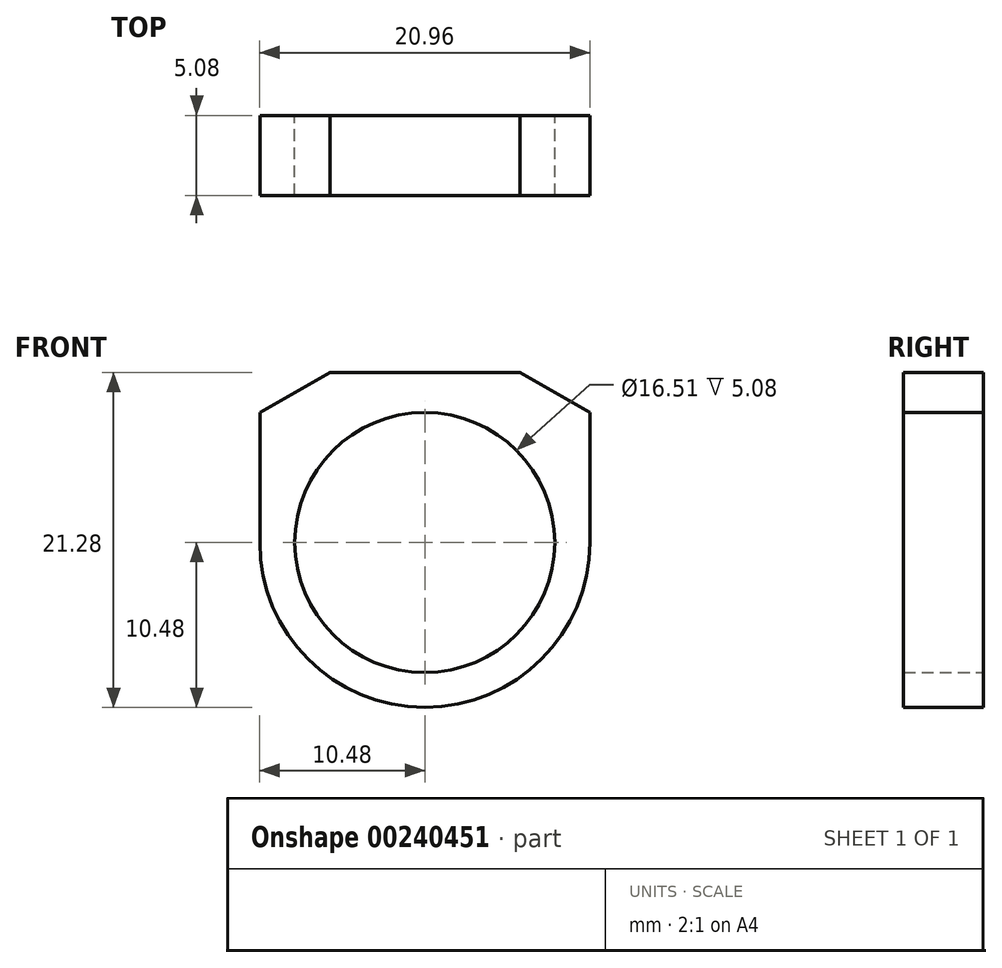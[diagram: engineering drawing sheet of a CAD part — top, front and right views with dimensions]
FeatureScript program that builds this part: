
annotation { "Feature Type Name" : "Feature", "Feature Type Description" : "" }
export const myFeature = defineFeature(function(context is Context, id is Id, definition is map)
    precondition{}
    {
        {
            var Q0;
            Q0=qCreatedBy(makeId("Front.planeOp"),FACE);
            var sketch = newSketch(context, id + "F0", { "sketchPlane" : qUnion([Q0])});
            skCircle(sketch, "E0", {"center": v(0, 0) * mm, "radius": 8.26 * mm});
            skCircle(sketch, "E1", {"center": v(0, 0) * mm, "radius": 10.48 * mm});
            skLineSegment(sketch, "E2", {"start": v(-10.48, 0) * mm, "end": v(-10.48, 8.26) * mm});
            skLineSegment(sketch, "E3", {"start": v(10.48, 0) * mm, "end": v(10.48, 8.26) * mm});
            skLineSegment(sketch, "E4", {"start": v(-10.48, 8.26) * mm, "end": v(-6.03, 10.8) * mm});
            skLineSegment(sketch, "E5", {"start": v(-6.03, 10.8) * mm, "end": v(6.03, 10.8) * mm});
            skLineSegment(sketch, "E6", {"start": v(6.03, 10.8) * mm, "end": v(10.48, 8.26) * mm});
            skSolve(sketch);
        }
        {
            var Q0;
            {var subQ1=sQuery(id+"F0.wireOp",EDGE,"E2");Q0=makeQuery(id+"F0.imprint","IMPRINT",FACE,{"disambiguationData":[TD([[makeQuery(id+"F0.imprint","IMPRINT",EDGE,{"derivedFrom":subQ1}),-1.0]])]});}
            var Q1;
            Q1=makeQuery(id+"F0.imprint","IMPRINT",FACE,{"disambiguationData":[TD([[makeQuery(id+"F0.imprint","IMPRINT",EDGE,{"derivedFrom":sQuery(id+"F0.wireOp",EDGE,"E0")}),-1.0]])]});
            extrude(context, id + "F1", {"entities" : qUnion([Q0, Q1]), "depth" : 5.08 * mm});
        }
    });
